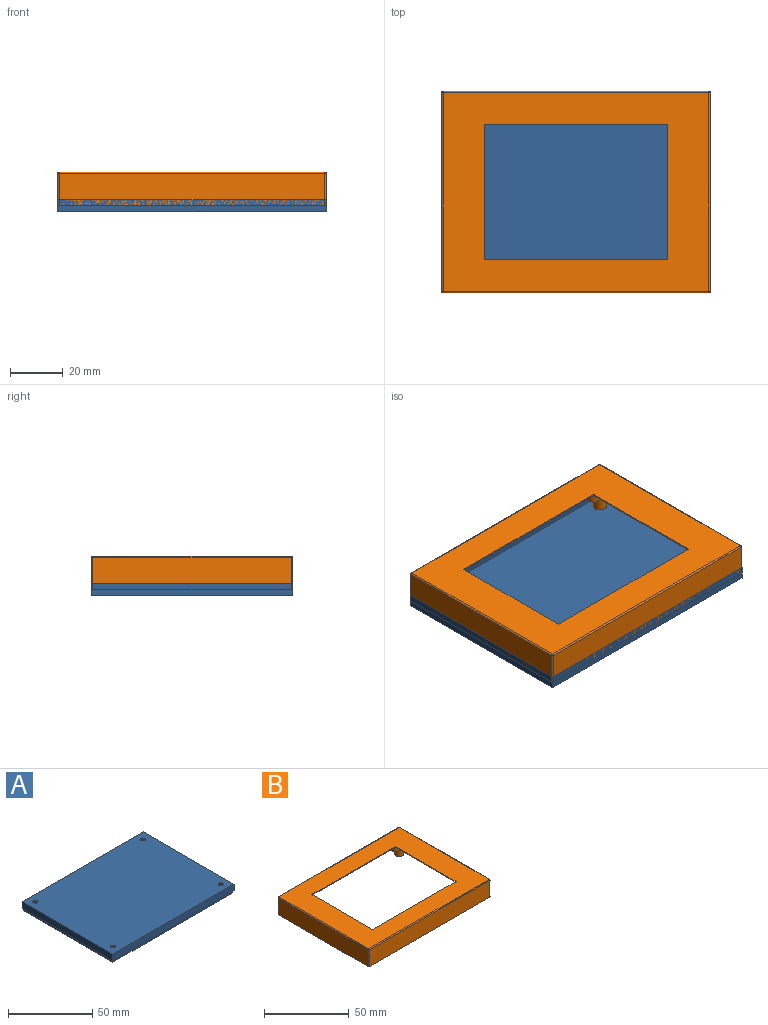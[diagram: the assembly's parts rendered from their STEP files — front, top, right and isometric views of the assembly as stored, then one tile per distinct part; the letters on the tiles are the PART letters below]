
ASSEMBLY  parts=2 mates=1
PART A: 20 faces, bbox 101.6x76.2x6.4 mm
  f0: plane 100.58x75.18mm, normal (0,0,-1), area 177.5mm2, adj f1,f2,f3,f4,f6,f7,f8,f9
  f1: plane 99.57x5.33mm, normal (0,-1,0), area 531.1mm2, adj f0,f2,f4,f5
  f2: plane 74.17x5.33mm, normal (1,0,0), area 395.6mm2, adj f0,f1,f3,f5
  f3: plane 99.57x5.33mm, normal (0,1,0), area 531.1mm2, adj f0,f2,f4,f5
  f4: plane 74.17x5.33mm, normal (-1,0,0), area 395.6mm2, adj f0,f1,f3,f5
  f5: plane 99.57x74.17mm, normal (0,0,-1), area 7358.4mm2, adj f1,f2,f3,f4,f16,f17,f18,f19
  f6: plane 75.18x1.52mm, normal (-1,0,0), area 114.6mm2, adj f0,f7,f9,f10
  f7: plane 100.58x1.52mm, normal (0,1,0), area 153.3mm2, adj f0,f6,f8,f10
  f8: plane 75.18x1.52mm, normal (1,0,0), area 114.6mm2, adj f0,f7,f9,f10
  f9: plane 100.58x1.52mm, normal (0,-1,0), area 153.3mm2, adj f0,f6,f8,f10
  f10: plane 101.6x76.2mm, normal (0,0,-1), area 179.6mm2, adj f6,f7,f8,f9,f12,f13,f14,f15
  f11: plane 101.6x76.2mm, normal (0,0,1), area 7715.6mm2, adj f12,f13,f14,f15,f16,f17,f18,f19
  f12: plane 76.2x4.83mm, normal (1,0,0), area 367.7mm2, adj f10,f11,f13,f15
  f13: plane 101.6x4.83mm, normal (0,-1,0), area 490.3mm2, adj f10,f11,f12,f14
  f14: plane 76.2x4.83mm, normal (-1,0,0), area 367.7mm2, adj f10,f11,f13,f15
  f15: plane 101.6x4.83mm, normal (0,1,0), area 490.3mm2, adj f10,f11,f12,f14
  f16: cylinder r=1.45mm len=2.9mm, axis (0,0,-1), area 9.2mm2, adj f5,f11
  f17: cylinder r=1.45mm len=2.9mm, axis (0,0,-1), area 9.2mm2, adj f5,f11
  f18: cylinder r=1.45mm len=2.9mm, axis (0,0,-1), area 9.2mm2, adj f5,f11
  f19: cylinder r=1.45mm len=2.9mm, axis (0,0,-1), area 9.2mm2, adj f5,f11
PART B: 59 faces, bbox 101.6x76.2x14.2 mm
  f0: plane 101.6x76.2mm, normal (0,0,-1), area 179.4mm2, adj f1,f2,f3,f8,f10,f11,f12,f13
  f1: plane 100.58x12.19mm, normal (0,1,0), area 1226.3mm2, adj f0,f33,f39,f42
  f2: plane 75.18x12.19mm, normal (-1,0,0), area 916.6mm2, adj f0,f36,f40,f42
  f3: plane 100.58x12.19mm, normal (0,-1,0), area 1226.3mm2, adj f0,f31,f35,f36
  f4: plane 50.8x0.51mm, normal (1,0,0), area 25.8mm2, adj f5,f7,f9,f14
  f5: plane 69.6x0.51mm, normal (0,-1,0), area 35.4mm2, adj f4,f6,f9,f14
  f6: plane 50.8x0.51mm, normal (-1,0,0), area 25.8mm2, adj f5,f7,f9,f14
  f7: plane 69.6x0.51mm, normal (0,1,0), area 35.4mm2, adj f4,f6,f9,f14
  f8: plane 75.18x12.19mm, normal (1,0,0), area 916.6mm2, adj f0,f31,f33,f34
  f9: plane 100.58x75.18mm, normal (0,0,1), area 4026.8mm2, adj f4,f5,f6,f7,f34,f35,f39,f40
  f10: plane 100.58x12.19mm, normal (0,-1,0), area 1226.3mm2, adj f0,f11,f13,f14
  f11: plane 75.18x12.19mm, normal (1,0,0), area 916.6mm2, adj f0,f10,f12,f14
  f12: plane 100.58x12.19mm, normal (0,1,0), area 1226.3mm2, adj f0,f11,f13,f14
  f13: plane 75.18x12.19mm, normal (-1,0,0), area 916.6mm2, adj f0,f10,f12,f14
  f14: plane 100.58x75.18mm, normal (0,0,-1), area 3864.7mm2, adj f4,f5,f6,f7,f10,f11,f12,f13
  f15: cylinder r=1.09mm len=4.57mm, axis (0,0,-1), area 31.4mm2, adj f17,f18
  f16: cylinder r=2.54mm len=5.08mm, axis (0,0,-1), area 73mm2, adj f14,f17
  f17: plane 5.08x5.08mm, normal (0,0,-1), area 16.5mm2, adj f15,f16
  f18: plane 2.18x2.18mm, normal (0,0,-1), area 3.7mm2, adj f15
  f19: cylinder r=1.09mm len=4.57mm, axis (0,0,-1), area 31.4mm2, adj f21,f22
  f20: cylinder r=2.54mm len=5.08mm, axis (0,0,-1), area 73mm2, adj f14,f21
  f21: plane 5.08x5.08mm, normal (0,0,-1), area 16.5mm2, adj f19,f20
  f22: plane 2.18x2.18mm, normal (0,0,-1), area 3.7mm2, adj f19
  f23: cylinder r=1.09mm len=4.57mm, axis (0,0,-1), area 31.4mm2, adj f25,f26
  f24: cylinder r=2.54mm len=5.08mm, axis (0,0,-1), area 73mm2, adj f14,f25
  f25: plane 5.08x5.08mm, normal (0,0,-1), area 16.5mm2, adj f23,f24
  f26: plane 2.18x2.18mm, normal (0,0,-1), area 3.7mm2, adj f23
  f27: cylinder r=1.09mm len=4.57mm, axis (0,0,-1), area 31.4mm2, adj f29,f30
  f28: cylinder r=2.54mm len=5.08mm, axis (0,0,-1), area 73mm2, adj f14,f29
  f29: plane 5.08x5.08mm, normal (0,0,-1), area 16.5mm2, adj f27,f28
  f30: plane 2.18x2.18mm, normal (0,0,-1), area 3.7mm2, adj f27
  f31: cylinder r=0.51mm len=12.19mm, axis (0,0,1), area 9.7mm2, adj f0,f3,f8,f32
  f32: sphere r=0.51mm, area 0.4mm2, adj f31,f34,f35
  f33: cylinder r=0.51mm len=12.19mm, axis (0,0,-1), area 9.7mm2, adj f0,f1,f8,f37
  f34: cylinder r=0.51mm len=75.18mm, axis (0,-1,0), area 60mm2, adj f8,f9,f32,f37
  f35: cylinder r=0.51mm len=100.58mm, axis (-1,0,0), area 80.3mm2, adj f3,f9,f32,f38
  f36: cylinder r=0.51mm len=12.19mm, axis (0,0,-1), area 9.7mm2, adj f0,f2,f3,f38
  f37: sphere r=0.51mm, area 0.4mm2, adj f33,f34,f39
  f38: sphere r=0.51mm, area 0.4mm2, adj f35,f36,f40
  f39: cylinder r=0.51mm len=100.58mm, axis (1,0,0), area 80.3mm2, adj f1,f9,f37,f41
  f40: cylinder r=0.51mm len=75.18mm, axis (0,1,0), area 60mm2, adj f2,f9,f38,f41
  f41: sphere r=0.51mm, area 0.4mm2, adj f39,f40,f42
  f42: cylinder r=0.51mm len=12.19mm, axis (0,0,1), area 9.7mm2, adj f0,f1,f2,f41
  f43: cylinder r=1.09mm len=13.72mm, axis (0,0,-1), area 94.1mm2, adj f45,f46
  f44: cylinder r=2.54mm len=13.72mm, axis (0,0,-1), area 218.9mm2, adj f14,f45
  f45: plane 5.08x5.08mm, normal (0,0,-1), area 16.5mm2, adj f43,f44
  f46: plane 2.18x2.18mm, normal (0,0,-1), area 3.7mm2, adj f43
  f47: cylinder r=1.09mm len=13.72mm, axis (0,0,-1), area 94.1mm2, adj f49,f50
  f48: cylinder r=2.54mm len=13.72mm, axis (0,0,-1), area 218.9mm2, adj f14,f49
  f49: plane 5.08x5.08mm, normal (0,0,-1), area 16.5mm2, adj f47,f48
  f50: plane 2.18x2.18mm, normal (0,0,-1), area 3.7mm2, adj f47
  f51: cylinder r=1.09mm len=13.72mm, axis (0,0,-1), area 94.1mm2, adj f53,f54
  f52: cylinder r=2.54mm len=13.72mm, axis (0,0,-1), area 218.9mm2, adj f14,f53
  f53: plane 5.08x5.08mm, normal (0,0,-1), area 16.5mm2, adj f51,f52
  f54: plane 2.18x2.18mm, normal (0,0,-1), area 3.7mm2, adj f51
  f55: cylinder r=1.09mm len=13.72mm, axis (0,0,-1), area 94.1mm2, adj f57,f58
  f56: cylinder r=2.54mm len=13.72mm, axis (0,0,-1), area 218.9mm2, adj f14,f57
  f57: plane 5.08x5.08mm, normal (0,0,-1), area 16.5mm2, adj f55,f56
  f58: plane 2.18x2.18mm, normal (0,0,-1), area 3.7mm2, adj f55
PLACE A rot(axis=(0,-1,0),180deg) t=(0.25,0,1.5)mm
PLACE B rot(axis=(0,1,0),0deg) t=(0.25,0,-2.44)mm
MATE parallel B.f3 <-> A.f13  axis (0,-1,0) through (0.25,-38.1,-2.44)mm
